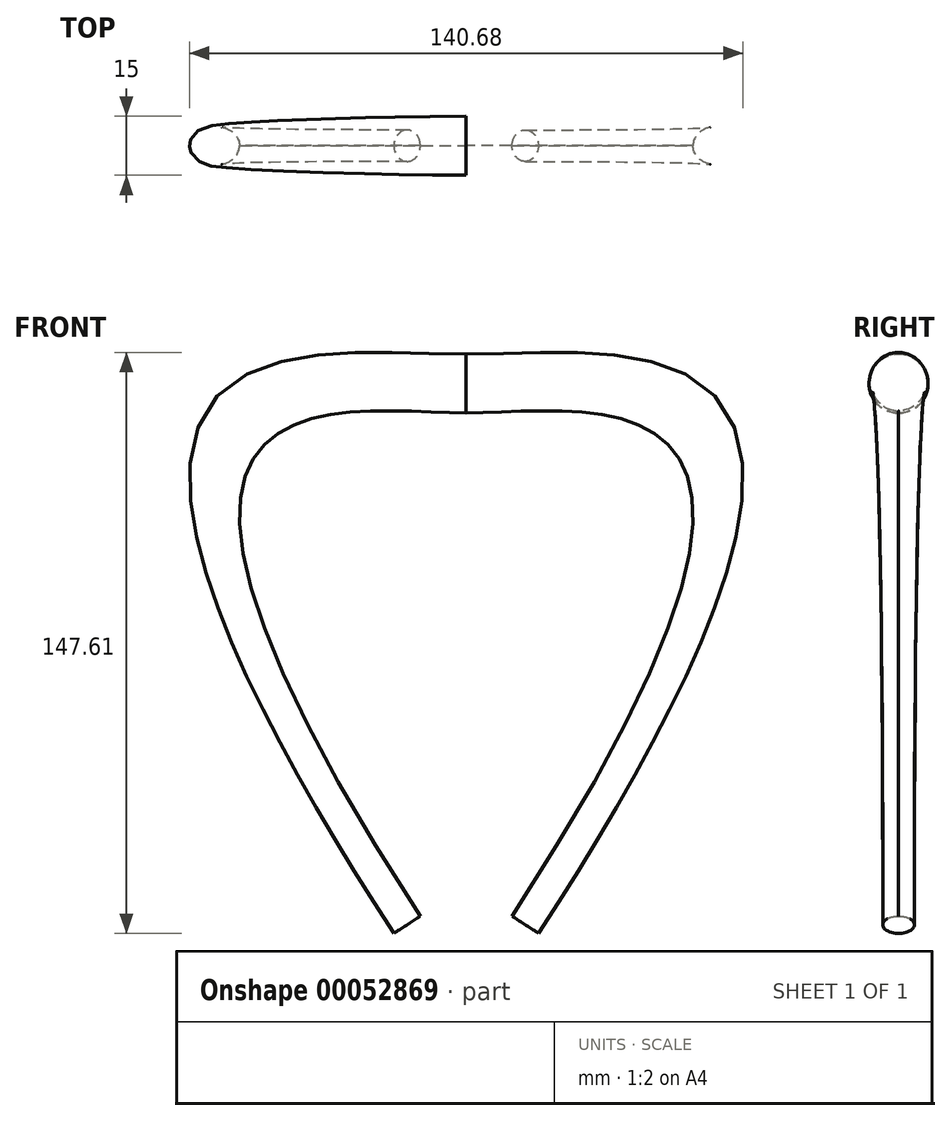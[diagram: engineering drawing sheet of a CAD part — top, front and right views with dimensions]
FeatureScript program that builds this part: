
annotation { "Feature Type Name" : "Feature", "Feature Type Description" : "" }
export const myFeature = defineFeature(function(context is Context, id is Id, definition is map)
    precondition{}
    {
        {
            var Q0;
            Q0=qCreatedBy(makeId("Front.planeOp"),FACE);
            var sketch = newSketch(context, id + "F0", { "sketchPlane" : qUnion([Q0])});
            skFitSpline(sketch, "E0", {"points": [v(-15, 0) * mm, v(-32.9, 30.38) * mm, v(-46.17, 58.56) * mm, v(-52.5, 91.67) * mm, v(-47.66, 113.44) * mm, v(-30.16, 130.97) * mm, v(0, 137.5) * mm], "startDerivative": vector(-72.3, 110.97) * mm, "endDerivative": vector(102, 0) * mm});
            skFitSpline(sketch, "E1.MirrorCS", {"points": [v(15, 0) * mm, v(32.9, 30.38) * mm, v(46.17, 58.56) * mm, v(52.5, 91.67) * mm, v(47.66, 113.44) * mm, v(30.16, 130.97) * mm, v(0, 137.5) * mm], "startDerivative": vector(72.3, 110.97) * mm, "endDerivative": vector(-102, 0) * mm});
            skLineSegment(sketch, "E2", {"start": v(0, 137.5) * mm, "end": v(69.37, 137.5) * mm, "construction": true});
            skSolve(sketch);
        }
        {
            var Q0;
            Q0=sQuery(id+"F0.wireOp",EDGE,"E0");
            var Q1;
            Q1=sQuery(id+"F0.wireOp",VERTEX,"E0.start");
            cPlane(context, id + "F1", {"entities" : qUnion([Q0, Q1]), "cplaneType" : CPlaneType.CURVE_POINT, "offset" : 150 * mm, "width" : 150 * mm, "height" : 150 * mm});
        }
        {
            var Q0;
            Q0=sQuery(id+"F0.wireOp",EDGE,"E0");
            var Q1;
            Q1=sQuery(id+"F0.wireOp",VERTEX,"E0.6.internal");
            cPlane(context, id + "F2", {"entities" : qUnion([Q0, Q1]), "cplaneType" : CPlaneType.CURVE_POINT, "offset" : 150 * mm, "width" : 150 * mm, "height" : 150 * mm});
        }
        {
            var Q0;
            Q0=qCreatedBy(id+"F1.planeOp",FACE);
            var sketch = newSketch(context, id + "F3", { "sketchPlane" : qUnion([Q0])});
            skCircle(sketch, "E3", {"center": v(-12.57, 0) * mm, "radius": 4 * mm});
            skSolve(sketch);
        }
        {
            var Q0;
            Q0=qCreatedBy(id+"F2.planeOp",FACE);
            var sketch = newSketch(context, id + "F4", { "sketchPlane" : qUnion([Q0])});
            skCircle(sketch, "E4", {"center": v(0, 137.5) * mm, "radius": 7.5 * mm});
            skSolve(sketch);
        }
        {
            var Q0;
            Q0=sQuery(id+"F3.wireOp",EDGE,"E3");
            var Q1;
            Q1=sQuery(id+"F4.wireOp",EDGE,"E4");
            var Q2;
            Q2=sQuery(id+"F0.wireOp",EDGE,"E0");
            loft(context, id + "F5", {"bodyType" : ToolBodyType.SURFACE, "startCondition" : LoftEndDerivativeType.NORMAL_TO_PROFILE, "startMagnitude" : 5, "endCondition" : LoftEndDerivativeType.NORMAL_TO_PROFILE, "endMagnitude" : 4, "wireProfilesArray" : [{ "wireProfileEntities" : qUnion([Q0]) }, { "wireProfileEntities" : qUnion([Q1]) }], "guidesArray" : [{ "guideEntities" : qUnion([Q2]), "guideDerivativeType" : LoftGuideDerivativeType.DEFAULT, "guideDerivativeMagnitude" : 1 }]});
        }
        {
            var Q0;
            Q0=makeQuery(id+"F5.opLoft","SWEPT_BODY",BODY,{"disambiguationData":[OSD([sQuery(id+"F3.wireOp",EDGE,"E3"),sQuery(id+"F4.wireOp",EDGE,"E4")])]});
            var Q1;
            Q1=qCreatedBy(makeId("Right.planeOp"),FACE);
            mirror(context, id + "F6", {"entities" : qUnion([Q0]), "mirrorPlane" : qUnion([Q1])});
        }
    });
